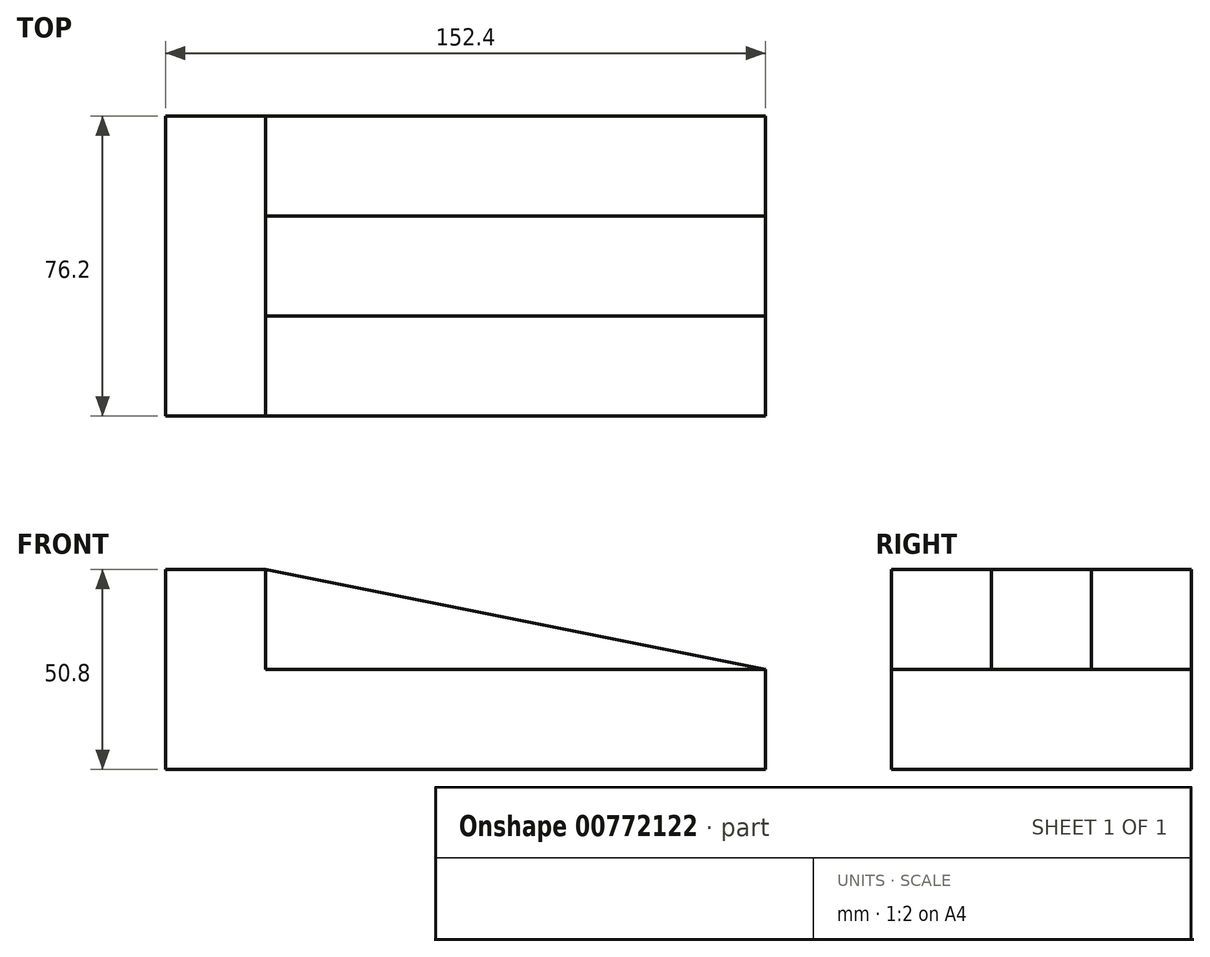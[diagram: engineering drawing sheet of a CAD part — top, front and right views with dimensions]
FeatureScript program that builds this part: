
annotation { "Feature Type Name" : "Feature", "Feature Type Description" : "" }
export const myFeature = defineFeature(function(context is Context, id is Id, definition is map)
    precondition{}
    {
        {
            var Q0;
            Q0=qCreatedBy(makeId("Front.planeOp"),FACE);
            var sketch = newSketch(context, id + "F0", { "sketchPlane" : qUnion([Q0])});
            skLineSegment(sketch, "E0", {"start": v(0, 0) * mm, "end": v(152.4, 0) * mm});
            skLineSegment(sketch, "E1", {"start": v(152.4, 0) * mm, "end": v(152.4, 50.8) * mm});
            skLineSegment(sketch, "E2", {"start": v(152.4, 50.8) * mm, "end": v(0, 50.8) * mm});
            skLineSegment(sketch, "E3", {"start": v(0, 50.8) * mm, "end": v(0, 0) * mm});
            skSolve(sketch);
        }
        {
            var Q0;
            Q0=makeQuery(id+"F0.imprint","IMPRINT",FACE,{"disambiguationData":[TD([[makeQuery(id+"F0.imprint","IMPRINT",EDGE,{"derivedFrom":sQuery(id+"F0.wireOp",EDGE,"E0")}),1.0]])]});
            extrude(context, id + "F1", {"entities" : qUnion([Q0]), "depth" : 76.2 * mm, "offsetDistance" : 25.4 * mm});
        }
        {
            var Q0;
            Q0=makeQuery(id+"F1.opExtrude","SWEPT_FACE",FACE,{"disambiguationData":[OSD([sQuery(id+"F0.wireOp",EDGE,"E2")])]});
            var sketch = newSketch(context, id + "F2", { "sketchPlane" : qUnion([Q0])});
            skLineSegment(sketch, "E4", {"start": v(152.4, -76.2) * mm, "end": v(152.4, -50.8) * mm});
            skLineSegment(sketch, "E5", {"start": v(152.4, -50.8) * mm, "end": v(25.4, -50.8) * mm});
            skLineSegment(sketch, "E6", {"start": v(25.4, -50.8) * mm, "end": v(25.4, -76.2) * mm});
            skLineSegment(sketch, "E7", {"start": v(25.4, -76.2) * mm, "end": v(152.4, -76.2) * mm});
            skSolve(sketch);
        }
        {
            var Q0;
            Q0=makeQuery(id+"F2.imprint","IMPRINT",FACE,{"disambiguationData":[TD([[makeQuery(id+"F2.imprint","IMPRINT",EDGE,{"derivedFrom":sQuery(id+"F2.wireOp",EDGE,"E4")}),1.0]])]});
            extrude(context, id + "F3", {"entities" : qUnion([Q0]), "operationType" : NewBodyOperationType.REMOVE, "oppositeDirection" : true, "depth" : 25.4 * mm, "offsetDistance" : 25.4 * mm});
        }
        {
            var Q0;
            Q0=makeQuery(id+"F1.opExtrude","SWEPT_FACE",FACE,{"disambiguationData":[OSD([sQuery(id+"F0.wireOp",EDGE,"E2")])]});
            var sketch = newSketch(context, id + "F4", { "sketchPlane" : qUnion([Q0])});
            skLineSegment(sketch, "E8", {"start": v(152.4, 0) * mm, "end": v(152.4, -25.4) * mm});
            skLineSegment(sketch, "E9", {"start": v(152.4, -25.4) * mm, "end": v(25.4, -25.4) * mm});
            skLineSegment(sketch, "E10", {"start": v(25.4, -25.4) * mm, "end": v(25.4, 0) * mm});
            skLineSegment(sketch, "E11", {"start": v(25.4, 0) * mm, "end": v(152.4, 0) * mm});
            skSolve(sketch);
        }
        {
            var Q0;
            Q0=makeQuery(id+"F4.imprint","IMPRINT",FACE,{"disambiguationData":[TD([[makeQuery(id+"F4.imprint","IMPRINT",EDGE,{"derivedFrom":sQuery(id+"F4.wireOp",EDGE,"E8")}),1.0]])]});
            extrude(context, id + "F5", {"entities" : qUnion([Q0]), "operationType" : NewBodyOperationType.REMOVE, "oppositeDirection" : true, "depth" : 25.4 * mm, "offsetDistance" : 25.4 * mm});
        }
        {
            var Q0;
            Q0=makeQuery(id+"F3.boolean.opBoolean","COPY",FACE,{"derivedFrom":makeQuery(id+"F3.opExtrude","SWEPT_FACE",FACE,{"disambiguationData":[OSD([sQuery(id+"F2.wireOp",EDGE,"E5")])]})});
            var sketch = newSketch(context, id + "F6", { "sketchPlane" : qUnion([Q0])});
            skLineSegment(sketch, "E12", {"start": v(152.4, 25.4) * mm, "end": v(25.4, 50.8) * mm});
            skLineSegment(sketch, "E13", {"start": v(25.4, 50.8) * mm, "end": v(152.4, 50.8) * mm});
            skLineSegment(sketch, "E14", {"start": v(152.4, 50.8) * mm, "end": v(152.4, 25.4) * mm});
            skSolve(sketch);
        }
        {
            var Q0;
            Q0=makeQuery(id+"F6.imprint","IMPRINT",FACE,{"disambiguationData":[TD([[makeQuery(id+"F6.imprint","IMPRINT",EDGE,{"derivedFrom":sQuery(id+"F6.wireOp",EDGE,"E12")}),-1.0]])]});
            extrude(context, id + "F7", {"entities" : qUnion([Q0]), "operationType" : NewBodyOperationType.REMOVE, "oppositeDirection" : true, "depth" : 25.4 * mm, "offsetDistance" : 25.4 * mm});
        }
    });
